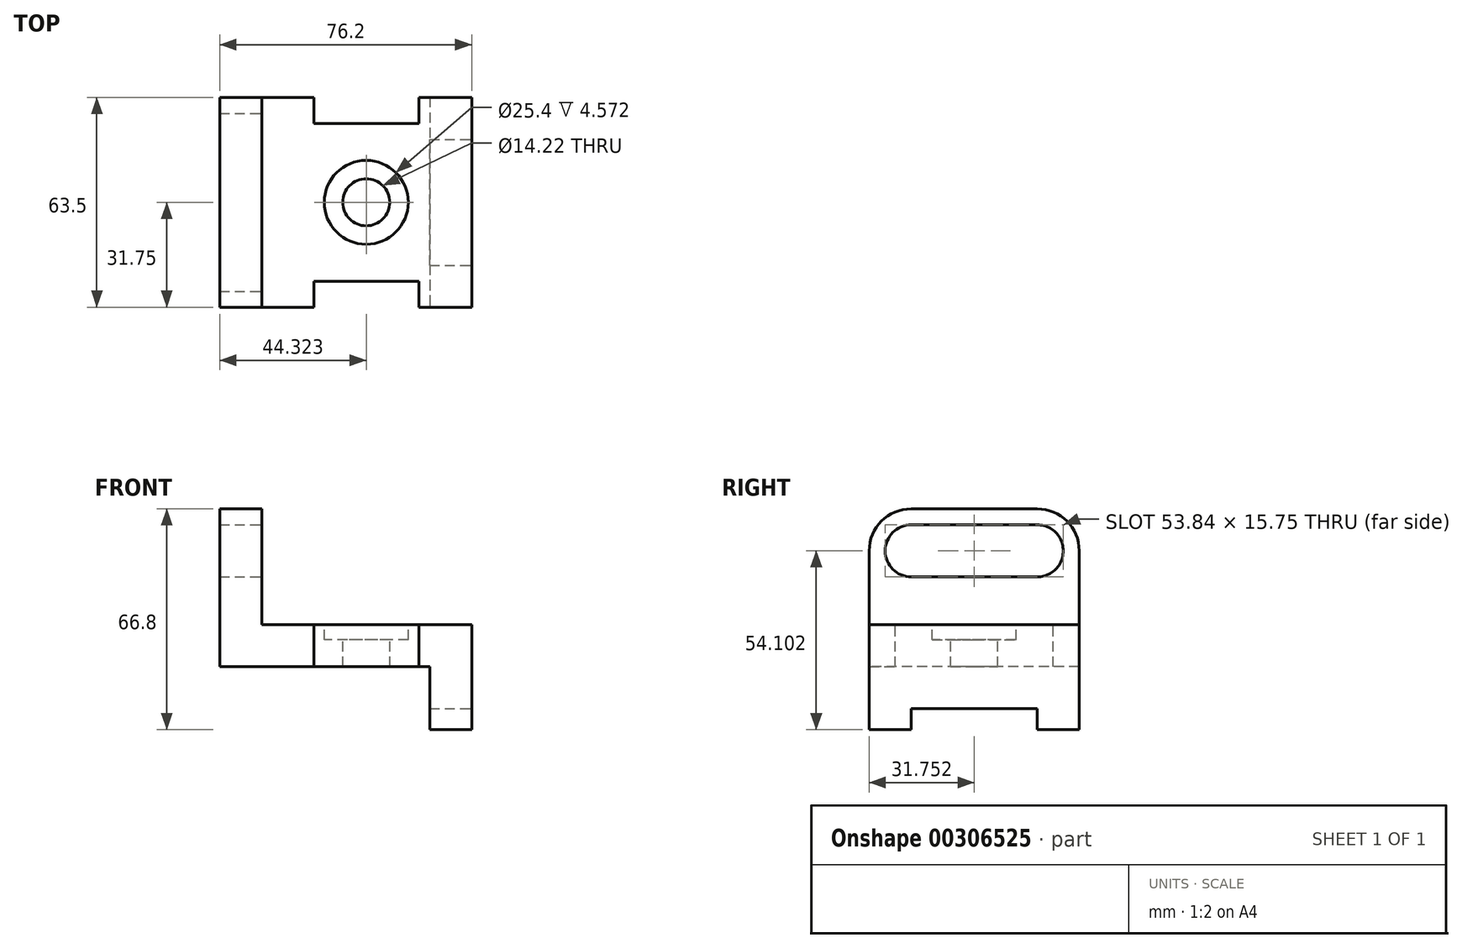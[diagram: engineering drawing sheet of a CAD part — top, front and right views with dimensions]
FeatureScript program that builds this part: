
annotation { "Feature Type Name" : "Feature", "Feature Type Description" : "" }
export const myFeature = defineFeature(function(context is Context, id is Id, definition is map)
    precondition{}
    {
        {
            var Q0;
            Q0=qCreatedBy(makeId("Top.planeOp"),FACE);
            var sketch = newSketch(context, id + "F0", { "sketchPlane" : qUnion([Q0])});
            skLineSegment(sketch, "E0.bottom", {"start": v(0, 0) * mm, "end": v(76.2, 0) * mm});
            skLineSegment(sketch, "E0.top", {"start": v(0, 63.5) * mm, "end": v(76.2, 63.5) * mm});
            skLineSegment(sketch, "E0.left", {"start": v(0, 0) * mm, "end": v(0, 63.5) * mm});
            skLineSegment(sketch, "E0.right", {"start": v(76.2, 0) * mm, "end": v(76.2, 63.5) * mm});
            skSolve(sketch);
        }
        {
            var Q0;
            Q0 = qSketchRegion(id + "F0", true);
            extrude(context, id + "F1", {"entities" : qUnion([Q0]), "depth" : 66.8 * mm});
        }
        {
            var Q0;
            Q0=makeQuery(id+"F1.opExtrude","SWEPT_FACE",FACE,{"disambiguationData":[OSD([sQuery(id+"F0.wireOp",EDGE,"E0.bottom")])]});
            var sketch = newSketch(context, id + "F2", { "sketchPlane" : qUnion([Q0])});
            skLineSegment(sketch, "E1.bottom", {"start": v(12.7, 66.8) * mm, "end": v(76.2, 66.8) * mm});
            skLineSegment(sketch, "E1.top", {"start": v(12.7, 31.75) * mm, "end": v(76.2, 31.75) * mm});
            skLineSegment(sketch, "E1.left", {"start": v(12.7, 66.8) * mm, "end": v(12.7, 31.75) * mm});
            skLineSegment(sketch, "E1.right", {"start": v(76.2, 66.8) * mm, "end": v(76.2, 31.75) * mm});
            skLineSegment(sketch, "E2.bottom", {"start": v(63.5, 0) * mm, "end": v(0, 0) * mm});
            skLineSegment(sketch, "E2.top", {"start": v(63.5, 19.05) * mm, "end": v(0, 19.05) * mm});
            skLineSegment(sketch, "E2.left", {"start": v(63.5, 0) * mm, "end": v(63.5, 19.05) * mm});
            skLineSegment(sketch, "E2.right", {"start": v(0, 0) * mm, "end": v(0, 19.05) * mm});
            skSolve(sketch);
        }
        {
            var Q0;
            Q0 = qSketchRegion(id + "F2", true);
            extrude(context, id + "F3", {"entities" : qUnion([Q0]), "operationType" : NewBodyOperationType.REMOVE, "endBound" : BoundingType.THROUGH_ALL, "oppositeDirection" : true, "depth" : 25.4 * mm});
        }
        {
            var Q0;
            Q0=makeQuery(id+"F1.opExtrude","CAP_EDGE",EDGE,{"disambiguationData":[OSD([sQuery(id+"F0.wireOp",EDGE,"E0.bottom")])],"isStart":false});
            var Q1;
            Q1=makeQuery(id+"F1.opExtrude","CAP_EDGE",EDGE,{"disambiguationData":[OSD([sQuery(id+"F0.wireOp",EDGE,"E0.top")])],"isStart":false});
            fillet(context, id + "F4", {"entities" : qUnion([Q0, Q1]), "radius" : 12.7 * mm, "tangentPropagation" : true, "allowEdgeOverflow" : false});
        }
        {
            var Q0;
            Q0=makeQuery(id+"F1.opExtrude","SWEPT_FACE",FACE,{"disambiguationData":[OSD([sQuery(id+"F0.wireOp",EDGE,"E0.right")])]});
            var sketch = newSketch(context, id + "F5", { "sketchPlane" : qUnion([Q0])});
            skLineSegment(sketch, "E3", {"start": v(12.7, 0) * mm, "end": v(12.7, 6.35) * mm});
            skLineSegment(sketch, "E4", {"start": v(12.7, 6.35) * mm, "end": v(50.8, 6.35) * mm});
            skLineSegment(sketch, "E5", {"start": v(50.8, 6.35) * mm, "end": v(50.8, 0) * mm});
            skLineSegment(sketch, "E6", {"start": v(50.8, 0) * mm, "end": v(12.7, 0) * mm});
            skSolve(sketch);
        }
        {
            var Q0;
            Q0 = qSketchRegion(id + "F5", true);
            extrude(context, id + "F6", {"entities" : qUnion([Q0]), "operationType" : NewBodyOperationType.REMOVE, "endBound" : BoundingType.THROUGH_ALL, "oppositeDirection" : true, "depth" : 25.4 * mm});
        }
        {
            var Q0;
            Q0=makeQuery(id+"F3.boolean.opBoolean","COPY",FACE,{"derivedFrom":makeQuery(id+"F3.opExtrude","SWEPT_FACE",FACE,{"disambiguationData":[OSD([sQuery(id+"F2.wireOp",EDGE,"E1.left")])]})});
            var sketch = newSketch(context, id + "F7", { "sketchPlane" : qUnion([Q0])});
            skArc(sketch, "E7", {"start": v(12.7, 61.97) * mm, "mid": v(4.83, 54.1) * mm, "end": v(12.7, 46.23) * mm});
            skArc(sketch, "E8", {"start": v(50.8, 46.23) * mm, "mid": v(58.67, 54.1) * mm, "end": v(50.8, 61.98) * mm});
            skLineSegment(sketch, "E9", {"start": v(12.7, 61.97) * mm, "end": v(50.8, 61.98) * mm});
            skLineSegment(sketch, "E10", {"start": v(50.8, 46.23) * mm, "end": v(12.7, 46.23) * mm});
            skSolve(sketch);
        }
        {
            var Q0;
            Q0 = qSketchRegion(id + "F7", true);
            extrude(context, id + "F8", {"entities" : qUnion([Q0]), "operationType" : NewBodyOperationType.REMOVE, "endBound" : BoundingType.THROUGH_ALL, "oppositeDirection" : true, "depth" : 25.4 * mm});
        }
        {
            var Q0;
            Q0=makeQuery(id+"F3.boolean.opBoolean","COPY",FACE,{"derivedFrom":makeQuery(id+"F3.opExtrude","SWEPT_FACE",FACE,{"disambiguationData":[OSD([sQuery(id+"F2.wireOp",EDGE,"E1.top")])]})});
            var sketch = newSketch(context, id + "F9", { "sketchPlane" : qUnion([Q0])});
            skLineSegment(sketch, "E11.bottom", {"start": v(28.45, 63.5) * mm, "end": v(60.2, 63.5) * mm});
            skLineSegment(sketch, "E11.top", {"start": v(28.45, 55.63) * mm, "end": v(60.2, 55.63) * mm});
            skLineSegment(sketch, "E11.left", {"start": v(28.45, 63.5) * mm, "end": v(28.45, 55.63) * mm});
            skLineSegment(sketch, "E11.right", {"start": v(60.2, 63.5) * mm, "end": v(60.2, 55.63) * mm});
            skLineSegment(sketch, "E12.bottom", {"start": v(60.2, 0) * mm, "end": v(28.45, 0) * mm});
            skLineSegment(sketch, "E12.top", {"start": v(60.2, 7.87) * mm, "end": v(28.45, 7.87) * mm});
            skLineSegment(sketch, "E12.left", {"start": v(60.2, 0) * mm, "end": v(60.2, 7.87) * mm});
            skLineSegment(sketch, "E12.right", {"start": v(28.45, 0) * mm, "end": v(28.45, 7.87) * mm});
            skSolve(sketch);
        }
        {
            var Q0;
            Q0 = qSketchRegion(id + "F9", true);
            extrude(context, id + "F10", {"entities" : qUnion([Q0]), "operationType" : NewBodyOperationType.REMOVE, "endBound" : BoundingType.THROUGH_ALL, "oppositeDirection" : true, "depth" : 25.4 * mm});
        }
        {
            var Q0;
            Q0=makeQuery(id+"F3.boolean.opBoolean","COPY",FACE,{"derivedFrom":makeQuery(id+"F3.opExtrude","SWEPT_FACE",FACE,{"disambiguationData":[OSD([sQuery(id+"F2.wireOp",EDGE,"E1.top")])]})});
            var sketch = newSketch(context, id + "F11", { "sketchPlane" : qUnion([Q0])});
            skCircle(sketch, "E13", {"center": v(44.32, 31.75) * mm, "radius": 12.7 * mm});
            skLineSegment(sketch, "E14", {"start": v(76.2, 31.75) * mm, "end": v(-27.62, 31.75) * mm, "construction": true});
            skPoint(sketch, "E14.endSnap0", {"position": v(76.2, 31.75) * mm});
            skLineSegment(sketch, "E15", {"start": v(44.32, 55.63) * mm, "end": v(44.32, -11.07) * mm, "construction": true});
            skSolve(sketch);
        }
        {
            var Q0;
            Q0 = qSketchRegion(id + "F11", true);
            extrude(context, id + "F12", {"entities" : qUnion([Q0]), "operationType" : NewBodyOperationType.REMOVE, "oppositeDirection" : true, "depth" : 4.57 * mm});
        }
        {
            var Q0;
            Q0=makeQuery(id+"F12.boolean.opBoolean","COPY",FACE,{"derivedFrom":makeQuery(id+"F12.opExtrude","CAP_FACE",FACE,{"disambiguationData":[OSD([sQuery(id+"F11.wireOp",EDGE,"E13")])],"isStart":false})});
            var sketch = newSketch(context, id + "F13", { "sketchPlane" : qUnion([Q0])});
            skCircle(sketch, "E16", {"center": v(44.32, 31.75) * mm, "radius": 7.11 * mm});
            skSolve(sketch);
        }
        {
            var Q0;
            Q0 = qSketchRegion(id + "F13", true);
            extrude(context, id + "F14", {"entities" : qUnion([Q0]), "operationType" : NewBodyOperationType.REMOVE, "endBound" : BoundingType.THROUGH_ALL, "oppositeDirection" : true, "depth" : 25.4 * mm});
        }
    });
